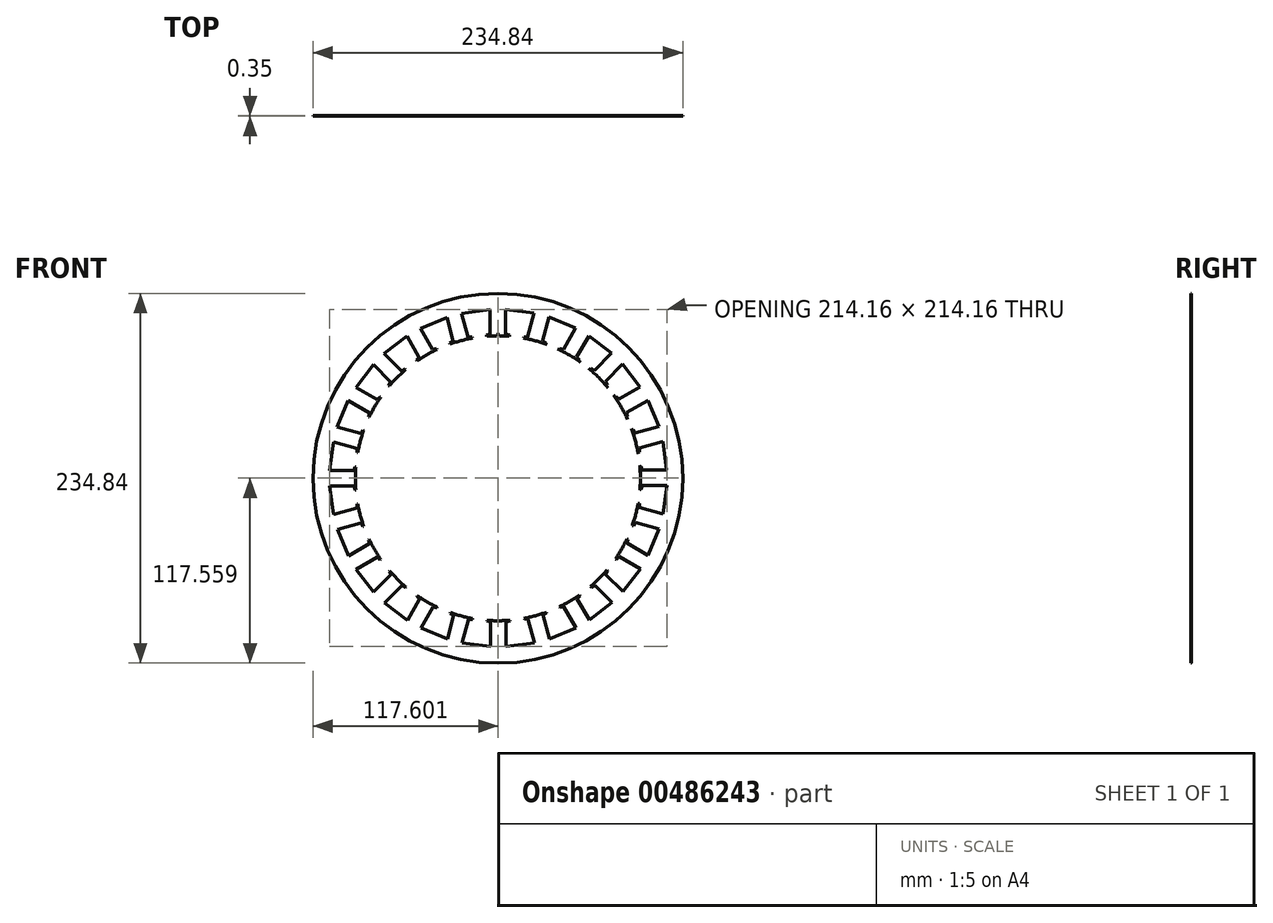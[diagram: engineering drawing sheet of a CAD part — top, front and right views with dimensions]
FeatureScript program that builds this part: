
annotation { "Feature Type Name" : "Feature", "Feature Type Description" : "" }
export const myFeature = defineFeature(function(context is Context, id is Id, definition is map)
    precondition{}
    {
        {
            var Q0;
            Q0=qCreatedBy(makeId("Front.planeOp"),FACE);
            var sketch = newSketch(context, id + "F0", { "sketchPlane" : qUnion([Q0])});
            skCircle(sketch, "E0", {"center": v(0, 0) * mm, "radius": 117.42 * mm});
            skCircle(sketch, "E1", {"center": v(0, 0) * mm, "radius": 90.5 * mm});
            skSolve(sketch);
        }
        {
            var Q0;
            Q0=makeQuery(id+"F0.imprint","IMPRINT",FACE,{"disambiguationData":[TD([[makeQuery(id+"F0.imprint","IMPRINT",EDGE,{"derivedFrom":sQuery(id+"F0.wireOp",EDGE,"E0")}),1.0]])]});
            extrude(context, id + "F1", {"entities" : qUnion([Q0]), "depth" : 0.35 * mm});
        }
        {
            var Q0;
            Q0=makeQuery(id+"F1.opExtrude","CAP_FACE",FACE,{"disambiguationData":[OSD([sQuery(id+"F0.wireOp",EDGE,"E0"),sQuery(id+"F0.wireOp",EDGE,"E1")])],"isStart":false});
            var sketch = newSketch(context, id + "F2", { "sketchPlane" : qUnion([Q0])});
            skLineSegment(sketch, "E2", {"start": v(0, 117.42) * mm, "end": v(0, 0) * mm, "construction": true});
            skLineSegment(sketch, "E3", {"start": v(0, 0) * mm, "end": v(15.9, 120.74) * mm, "construction": true});
            skLineSegment(sketch, "E4", {"start": v(7.35, 90.2) * mm, "end": v(7.35, 91) * mm});
            skLineSegment(sketch, "E5", {"start": v(7.35, 91) * mm, "end": v(4.94, 91.66) * mm});
            skLineSegment(sketch, "E6", {"start": v(4.94, 91.66) * mm, "end": v(4.94, 107.22) * mm});
            skLineSegment(sketch, "E7", {"start": v(4.94, 107.22) * mm, "end": v(13.96, 106.03) * mm});
            skLineSegment(sketch, "E8.MirrorCS", {"start": v(22.98, 104.85) * mm, "end": v(13.96, 106.03) * mm});
            skLineSegment(sketch, "E9.MirrorCS", {"start": v(18.95, 89.82) * mm, "end": v(22.98, 104.85) * mm});
            skLineSegment(sketch, "E10.MirrorCS", {"start": v(16.45, 89.8) * mm, "end": v(18.95, 89.82) * mm});
            skLineSegment(sketch, "E11.MirrorCS", {"start": v(16.25, 89.03) * mm, "end": v(16.45, 89.8) * mm});
            skLineSegment(sketch, "E12", {"start": v(7.35, 90.2) * mm, "end": v(16.25, 89.03) * mm});
            skLineSegment(sketch, "E13.1.0", {"start": v(-18.9, 89.77) * mm, "end": v(-22.94, 104.8) * mm});
            skLineSegment(sketch, "E13.1.1", {"start": v(-22.94, 104.8) * mm, "end": v(-13.92, 106) * mm});
            skLineSegment(sketch, "E13.1.2", {"start": v(-4.9, 107.18) * mm, "end": v(-13.92, 106) * mm});
            skLineSegment(sketch, "E13.1.3", {"start": v(-4.9, 91.62) * mm, "end": v(-4.9, 107.18) * mm});
            skLineSegment(sketch, "E13.1.4", {"start": v(-7.3, 90.96) * mm, "end": v(-4.9, 91.62) * mm});
            skLineSegment(sketch, "E13.1.5", {"start": v(-7.3, 90.16) * mm, "end": v(-7.3, 90.96) * mm});
            skLineSegment(sketch, "E13.1.6", {"start": v(-16.2, 88.99) * mm, "end": v(-7.3, 90.16) * mm});
            skLineSegment(sketch, "E13.1.7", {"start": v(-16.2, 88.99) * mm, "end": v(-16.41, 89.76) * mm});
            skLineSegment(sketch, "E13.1.8", {"start": v(-16.41, 89.76) * mm, "end": v(-18.9, 89.77) * mm});
            skLineSegment(sketch, "E13.2.0", {"start": v(-41.46, 81.78) * mm, "end": v(-49.24, 95.25) * mm});
            skLineSegment(sketch, "E13.2.1", {"start": v(-49.24, 95.25) * mm, "end": v(-40.83, 98.74) * mm});
            skLineSegment(sketch, "E13.2.2", {"start": v(-32.43, 102.22) * mm, "end": v(-40.83, 98.74) * mm});
            skLineSegment(sketch, "E13.2.3", {"start": v(-28.4, 87.19) * mm, "end": v(-32.43, 102.22) * mm});
            skLineSegment(sketch, "E13.2.4", {"start": v(-30.56, 85.93) * mm, "end": v(-28.4, 87.19) * mm});
            skLineSegment(sketch, "E13.2.5", {"start": v(-30.35, 85.15) * mm, "end": v(-30.56, 85.93) * mm});
            skLineSegment(sketch, "E13.2.6", {"start": v(-38.64, 81.72) * mm, "end": v(-30.35, 85.15) * mm});
            skLineSegment(sketch, "E13.2.7", {"start": v(-38.64, 81.72) * mm, "end": v(-39.04, 82.41) * mm});
            skLineSegment(sketch, "E13.2.8", {"start": v(-39.04, 82.41) * mm, "end": v(-41.46, 81.78) * mm});
            skLineSegment(sketch, "E13.3.0", {"start": v(-61.17, 68.22) * mm, "end": v(-72.17, 79.22) * mm});
            skLineSegment(sketch, "E13.3.1", {"start": v(-72.17, 79.22) * mm, "end": v(-64.96, 84.76) * mm});
            skLineSegment(sketch, "E13.3.2", {"start": v(-57.74, 90.3) * mm, "end": v(-64.96, 84.76) * mm});
            skLineSegment(sketch, "E13.3.3", {"start": v(-49.96, 76.82) * mm, "end": v(-57.74, 90.3) * mm});
            skLineSegment(sketch, "E13.3.4", {"start": v(-51.71, 75.05) * mm, "end": v(-49.96, 76.82) * mm});
            skLineSegment(sketch, "E13.3.5", {"start": v(-51.31, 74.35) * mm, "end": v(-51.71, 75.05) * mm});
            skLineSegment(sketch, "E13.3.6", {"start": v(-58.43, 68.9) * mm, "end": v(-51.31, 74.35) * mm});
            skLineSegment(sketch, "E13.3.7", {"start": v(-58.43, 68.9) * mm, "end": v(-59, 69.46) * mm});
            skLineSegment(sketch, "E13.3.8", {"start": v(-59, 69.46) * mm, "end": v(-61.17, 68.22) * mm});
            skLineSegment(sketch, "E13.4.0", {"start": v(-76.7, 50.02) * mm, "end": v(-90.18, 57.8) * mm});
            skLineSegment(sketch, "E13.4.1", {"start": v(-90.18, 57.8) * mm, "end": v(-84.64, 65.02) * mm});
            skLineSegment(sketch, "E13.4.2", {"start": v(-79.1, 72.24) * mm, "end": v(-84.64, 65.02) * mm});
            skLineSegment(sketch, "E13.4.3", {"start": v(-68.1, 61.23) * mm, "end": v(-79.1, 72.24) * mm});
            skLineSegment(sketch, "E13.4.4", {"start": v(-69.33, 59.06) * mm, "end": v(-68.1, 61.23) * mm});
            skLineSegment(sketch, "E13.4.5", {"start": v(-68.77, 58.5) * mm, "end": v(-69.33, 59.06) * mm});
            skLineSegment(sketch, "E13.4.6", {"start": v(-74.23, 51.38) * mm, "end": v(-68.77, 58.5) * mm});
            skLineSegment(sketch, "E13.4.7", {"start": v(-74.23, 51.38) * mm, "end": v(-74.92, 51.78) * mm});
            skLineSegment(sketch, "E13.4.8", {"start": v(-74.92, 51.78) * mm, "end": v(-76.7, 50.02) * mm});
            skLineSegment(sketch, "E13.5.0", {"start": v(-87, 28.42) * mm, "end": v(-102.02, 32.45) * mm});
            skLineSegment(sketch, "E13.5.1", {"start": v(-102.02, 32.45) * mm, "end": v(-98.54, 40.86) * mm});
            skLineSegment(sketch, "E13.5.2", {"start": v(-95.06, 49.26) * mm, "end": v(-98.54, 40.86) * mm});
            skLineSegment(sketch, "E13.5.3", {"start": v(-81.58, 41.48) * mm, "end": v(-95.06, 49.26) * mm});
            skLineSegment(sketch, "E13.5.4", {"start": v(-82.22, 39.06) * mm, "end": v(-81.58, 41.48) * mm});
            skLineSegment(sketch, "E13.5.5", {"start": v(-81.52, 38.66) * mm, "end": v(-82.22, 39.06) * mm});
            skLineSegment(sketch, "E13.5.6", {"start": v(-84.96, 30.37) * mm, "end": v(-81.52, 38.66) * mm});
            skLineSegment(sketch, "E13.5.7", {"start": v(-84.96, 30.37) * mm, "end": v(-85.73, 30.58) * mm});
            skLineSegment(sketch, "E13.5.8", {"start": v(-85.73, 30.58) * mm, "end": v(-87, 28.42) * mm});
            skLineSegment(sketch, "E13.6.0", {"start": v(-91.34, 4.9) * mm, "end": v(-106.9, 4.9) * mm});
            skLineSegment(sketch, "E13.6.1", {"start": v(-106.9, 4.9) * mm, "end": v(-105.71, 13.92) * mm});
            skLineSegment(sketch, "E13.6.2", {"start": v(-104.53, 22.94) * mm, "end": v(-105.71, 13.92) * mm});
            skLineSegment(sketch, "E13.6.3", {"start": v(-89.5, 18.9) * mm, "end": v(-104.53, 22.94) * mm});
            skLineSegment(sketch, "E13.6.4", {"start": v(-89.48, 16.41) * mm, "end": v(-89.5, 18.9) * mm});
            skLineSegment(sketch, "E13.6.5", {"start": v(-88.71, 16.2) * mm, "end": v(-89.48, 16.41) * mm});
            skLineSegment(sketch, "E13.6.6", {"start": v(-89.88, 7.3) * mm, "end": v(-88.71, 16.2) * mm});
            skLineSegment(sketch, "E13.6.7", {"start": v(-89.88, 7.3) * mm, "end": v(-90.68, 7.3) * mm});
            skLineSegment(sketch, "E13.6.8", {"start": v(-90.68, 7.3) * mm, "end": v(-91.34, 4.9) * mm});
            skLineSegment(sketch, "E13.7.0", {"start": v(-89.45, -18.95) * mm, "end": v(-104.48, -22.98) * mm});
            skLineSegment(sketch, "E13.7.1", {"start": v(-104.48, -22.98) * mm, "end": v(-105.67, -13.96) * mm});
            skLineSegment(sketch, "E13.7.2", {"start": v(-106.86, -4.94) * mm, "end": v(-105.67, -13.96) * mm});
            skLineSegment(sketch, "E13.7.3", {"start": v(-91.3, -4.94) * mm, "end": v(-106.86, -4.94) * mm});
            skLineSegment(sketch, "E13.7.4", {"start": v(-90.64, -7.35) * mm, "end": v(-91.3, -4.94) * mm});
            skLineSegment(sketch, "E13.7.5", {"start": v(-89.84, -7.35) * mm, "end": v(-90.64, -7.35) * mm});
            skLineSegment(sketch, "E13.7.6", {"start": v(-88.67, -16.25) * mm, "end": v(-89.84, -7.35) * mm});
            skLineSegment(sketch, "E13.7.7", {"start": v(-88.67, -16.25) * mm, "end": v(-89.44, -16.45) * mm});
            skLineSegment(sketch, "E13.7.8", {"start": v(-89.44, -16.45) * mm, "end": v(-89.45, -18.95) * mm});
            skLineSegment(sketch, "E13.8.0", {"start": v(-81.46, -41.5) * mm, "end": v(-94.93, -49.28) * mm});
            skLineSegment(sketch, "E13.8.1", {"start": v(-94.93, -49.28) * mm, "end": v(-98.42, -40.88) * mm});
            skLineSegment(sketch, "E13.8.2", {"start": v(-101.9, -32.47) * mm, "end": v(-98.42, -40.88) * mm});
            skLineSegment(sketch, "E13.8.3", {"start": v(-86.87, -28.44) * mm, "end": v(-101.9, -32.47) * mm});
            skLineSegment(sketch, "E13.8.4", {"start": v(-85.6, -30.6) * mm, "end": v(-86.87, -28.44) * mm});
            skLineSegment(sketch, "E13.8.5", {"start": v(-84.83, -30.4) * mm, "end": v(-85.6, -30.6) * mm});
            skLineSegment(sketch, "E13.8.6", {"start": v(-81.4, -38.68) * mm, "end": v(-84.83, -30.4) * mm});
            skLineSegment(sketch, "E13.8.7", {"start": v(-81.4, -38.68) * mm, "end": v(-82.1, -39.08) * mm});
            skLineSegment(sketch, "E13.8.8", {"start": v(-82.1, -39.08) * mm, "end": v(-81.46, -41.5) * mm});
            skLineSegment(sketch, "E13.9.0", {"start": v(-67.9, -61.21) * mm, "end": v(-78.9, -72.21) * mm});
            skLineSegment(sketch, "E13.9.1", {"start": v(-78.9, -72.21) * mm, "end": v(-84.44, -65) * mm});
            skLineSegment(sketch, "E13.9.2", {"start": v(-89.98, -57.78) * mm, "end": v(-84.44, -65) * mm});
            skLineSegment(sketch, "E13.9.3", {"start": v(-76.5, -50) * mm, "end": v(-89.98, -57.78) * mm});
            skLineSegment(sketch, "E13.9.4", {"start": v(-74.73, -51.76) * mm, "end": v(-76.5, -50) * mm});
            skLineSegment(sketch, "E13.9.5", {"start": v(-74.03, -51.36) * mm, "end": v(-74.73, -51.76) * mm});
            skLineSegment(sketch, "E13.9.6", {"start": v(-68.57, -58.48) * mm, "end": v(-74.03, -51.36) * mm});
            skLineSegment(sketch, "E13.9.7", {"start": v(-68.57, -58.48) * mm, "end": v(-69.14, -59.04) * mm});
            skLineSegment(sketch, "E13.9.8", {"start": v(-69.14, -59.04) * mm, "end": v(-67.9, -61.21) * mm});
            skLineSegment(sketch, "E13.10.0", {"start": v(-49.7, -76.74) * mm, "end": v(-57.48, -90.22) * mm});
            skLineSegment(sketch, "E13.10.1", {"start": v(-57.48, -90.22) * mm, "end": v(-64.7, -84.68) * mm});
            skLineSegment(sketch, "E13.10.2", {"start": v(-71.92, -79.14) * mm, "end": v(-64.7, -84.68) * mm});
            skLineSegment(sketch, "E13.10.3", {"start": v(-60.91, -68.14) * mm, "end": v(-71.92, -79.14) * mm});
            skLineSegment(sketch, "E13.10.4", {"start": v(-58.74, -69.38) * mm, "end": v(-60.91, -68.14) * mm});
            skLineSegment(sketch, "E13.10.5", {"start": v(-58.18, -68.81) * mm, "end": v(-58.74, -69.38) * mm});
            skLineSegment(sketch, "E13.10.6", {"start": v(-51.06, -74.27) * mm, "end": v(-58.18, -68.81) * mm});
            skLineSegment(sketch, "E13.10.7", {"start": v(-51.06, -74.27) * mm, "end": v(-51.46, -74.97) * mm});
            skLineSegment(sketch, "E13.10.8", {"start": v(-51.46, -74.97) * mm, "end": v(-49.7, -76.74) * mm});
            skLineSegment(sketch, "E13.11.0", {"start": v(-28.1, -87.03) * mm, "end": v(-32.13, -102.06) * mm});
            skLineSegment(sketch, "E13.11.1", {"start": v(-32.13, -102.06) * mm, "end": v(-40.54, -98.58) * mm});
            skLineSegment(sketch, "E13.11.2", {"start": v(-48.94, -95.1) * mm, "end": v(-40.54, -98.58) * mm});
            skLineSegment(sketch, "E13.11.3", {"start": v(-41.16, -81.62) * mm, "end": v(-48.94, -95.1) * mm});
            skLineSegment(sketch, "E13.11.4", {"start": v(-38.74, -82.26) * mm, "end": v(-41.16, -81.62) * mm});
            skLineSegment(sketch, "E13.11.5", {"start": v(-38.34, -81.57) * mm, "end": v(-38.74, -82.26) * mm});
            skLineSegment(sketch, "E13.11.6", {"start": v(-30.05, -85) * mm, "end": v(-38.34, -81.57) * mm});
            skLineSegment(sketch, "E13.11.7", {"start": v(-30.05, -85) * mm, "end": v(-30.26, -85.77) * mm});
            skLineSegment(sketch, "E13.11.8", {"start": v(-30.26, -85.77) * mm, "end": v(-28.1, -87.03) * mm});
            skLineSegment(sketch, "E13.12.0", {"start": v(-4.58, -91.38) * mm, "end": v(-4.58, -106.94) * mm});
            skLineSegment(sketch, "E13.12.1", {"start": v(-4.58, -106.94) * mm, "end": v(-13.6, -105.76) * mm});
            skLineSegment(sketch, "E13.12.2", {"start": v(-22.62, -104.57) * mm, "end": v(-13.6, -105.76) * mm});
            skLineSegment(sketch, "E13.12.3", {"start": v(-18.6, -89.54) * mm, "end": v(-22.62, -104.57) * mm});
            skLineSegment(sketch, "E13.12.4", {"start": v(-16.1, -89.53) * mm, "end": v(-18.6, -89.54) * mm});
            skLineSegment(sketch, "E13.12.5", {"start": v(-15.88, -88.75) * mm, "end": v(-16.1, -89.53) * mm});
            skLineSegment(sketch, "E13.12.6", {"start": v(-6.99, -89.92) * mm, "end": v(-15.88, -88.75) * mm});
            skLineSegment(sketch, "E13.12.7", {"start": v(-6.99, -89.92) * mm, "end": v(-6.99, -90.72) * mm});
            skLineSegment(sketch, "E13.12.8", {"start": v(-6.99, -90.72) * mm, "end": v(-4.58, -91.38) * mm});
            skLineSegment(sketch, "E13.13.0", {"start": v(19.27, -89.5) * mm, "end": v(23.3, -104.53) * mm});
            skLineSegment(sketch, "E13.13.1", {"start": v(23.3, -104.53) * mm, "end": v(14.28, -105.71) * mm});
            skLineSegment(sketch, "E13.13.2", {"start": v(5.26, -106.9) * mm, "end": v(14.28, -105.71) * mm});
            skLineSegment(sketch, "E13.13.3", {"start": v(5.26, -91.34) * mm, "end": v(5.26, -106.9) * mm});
            skLineSegment(sketch, "E13.13.4", {"start": v(7.67, -90.68) * mm, "end": v(5.26, -91.34) * mm});
            skLineSegment(sketch, "E13.13.5", {"start": v(7.67, -89.88) * mm, "end": v(7.67, -90.68) * mm});
            skLineSegment(sketch, "E13.13.6", {"start": v(16.57, -88.71) * mm, "end": v(7.67, -89.88) * mm});
            skLineSegment(sketch, "E13.13.7", {"start": v(16.57, -88.71) * mm, "end": v(16.77, -89.48) * mm});
            skLineSegment(sketch, "E13.13.8", {"start": v(16.77, -89.48) * mm, "end": v(19.27, -89.5) * mm});
            skLineSegment(sketch, "E13.14.0", {"start": v(41.82, -81.5) * mm, "end": v(49.6, -94.98) * mm});
            skLineSegment(sketch, "E13.14.1", {"start": v(49.6, -94.98) * mm, "end": v(41.2, -98.46) * mm});
            skLineSegment(sketch, "E13.14.2", {"start": v(32.8, -101.94) * mm, "end": v(41.2, -98.46) * mm});
            skLineSegment(sketch, "E13.14.3", {"start": v(28.76, -86.9) * mm, "end": v(32.8, -101.94) * mm});
            skLineSegment(sketch, "E13.14.4", {"start": v(30.92, -85.65) * mm, "end": v(28.76, -86.9) * mm});
            skLineSegment(sketch, "E13.14.5", {"start": v(30.71, -84.88) * mm, "end": v(30.92, -85.65) * mm});
            skLineSegment(sketch, "E13.14.6", {"start": v(39, -81.44) * mm, "end": v(30.71, -84.88) * mm});
            skLineSegment(sketch, "E13.14.7", {"start": v(39, -81.44) * mm, "end": v(39.4, -82.13) * mm});
            skLineSegment(sketch, "E13.14.8", {"start": v(39.4, -82.13) * mm, "end": v(41.82, -81.5) * mm});
            skLineSegment(sketch, "E13.15.0", {"start": v(61.53, -67.94) * mm, "end": v(72.53, -78.95) * mm});
            skLineSegment(sketch, "E13.15.1", {"start": v(72.53, -78.95) * mm, "end": v(65.32, -84.48) * mm});
            skLineSegment(sketch, "E13.15.2", {"start": v(58.1, -90.02) * mm, "end": v(65.32, -84.48) * mm});
            skLineSegment(sketch, "E13.15.3", {"start": v(50.32, -76.55) * mm, "end": v(58.1, -90.02) * mm});
            skLineSegment(sketch, "E13.15.4", {"start": v(52.08, -74.77) * mm, "end": v(50.32, -76.55) * mm});
            skLineSegment(sketch, "E13.15.5", {"start": v(51.68, -74.08) * mm, "end": v(52.08, -74.77) * mm});
            skLineSegment(sketch, "E13.15.6", {"start": v(58.8, -68.61) * mm, "end": v(51.68, -74.08) * mm});
            skLineSegment(sketch, "E13.15.7", {"start": v(58.8, -68.61) * mm, "end": v(59.36, -69.18) * mm});
            skLineSegment(sketch, "E13.15.8", {"start": v(59.36, -69.18) * mm, "end": v(61.53, -67.94) * mm});
            skLineSegment(sketch, "E13.16.0", {"start": v(77.06, -49.74) * mm, "end": v(90.54, -57.52) * mm});
            skLineSegment(sketch, "E13.16.1", {"start": v(90.54, -57.52) * mm, "end": v(85, -64.74) * mm});
            skLineSegment(sketch, "E13.16.2", {"start": v(79.46, -71.96) * mm, "end": v(85, -64.74) * mm});
            skLineSegment(sketch, "E13.16.3", {"start": v(68.46, -60.96) * mm, "end": v(79.46, -71.96) * mm});
            skLineSegment(sketch, "E13.16.4", {"start": v(69.7, -58.79) * mm, "end": v(68.46, -60.96) * mm});
            skLineSegment(sketch, "E13.16.5", {"start": v(69.13, -58.22) * mm, "end": v(69.7, -58.79) * mm});
            skLineSegment(sketch, "E13.16.6", {"start": v(74.6, -51.1) * mm, "end": v(69.13, -58.22) * mm});
            skLineSegment(sketch, "E13.16.7", {"start": v(74.6, -51.1) * mm, "end": v(75.29, -51.5) * mm});
            skLineSegment(sketch, "E13.16.8", {"start": v(75.29, -51.5) * mm, "end": v(77.06, -49.74) * mm});
            skLineSegment(sketch, "E13.17.0", {"start": v(87.35, -28.15) * mm, "end": v(102.38, -32.17) * mm});
            skLineSegment(sketch, "E13.17.1", {"start": v(102.38, -32.17) * mm, "end": v(98.9, -40.58) * mm});
            skLineSegment(sketch, "E13.17.2", {"start": v(95.42, -48.98) * mm, "end": v(98.9, -40.58) * mm});
            skLineSegment(sketch, "E13.17.3", {"start": v(81.94, -41.2) * mm, "end": v(95.42, -48.98) * mm});
            skLineSegment(sketch, "E13.17.4", {"start": v(82.58, -38.79) * mm, "end": v(81.94, -41.2) * mm});
            skLineSegment(sketch, "E13.17.5", {"start": v(81.89, -38.39) * mm, "end": v(82.58, -38.79) * mm});
            skLineSegment(sketch, "E13.17.6", {"start": v(85.32, -30.1) * mm, "end": v(81.89, -38.39) * mm});
            skLineSegment(sketch, "E13.17.7", {"start": v(85.32, -30.1) * mm, "end": v(86.1, -30.3) * mm});
            skLineSegment(sketch, "E13.17.8", {"start": v(86.1, -30.3) * mm, "end": v(87.35, -28.15) * mm});
            skLineSegment(sketch, "E13.18.0", {"start": v(91.7, -4.62) * mm, "end": v(107.26, -4.62) * mm});
            skLineSegment(sketch, "E13.18.1", {"start": v(107.26, -4.62) * mm, "end": v(106.08, -13.64) * mm});
            skLineSegment(sketch, "E13.18.2", {"start": v(104.89, -22.66) * mm, "end": v(106.08, -13.64) * mm});
            skLineSegment(sketch, "E13.18.3", {"start": v(89.86, -18.63) * mm, "end": v(104.89, -22.66) * mm});
            skLineSegment(sketch, "E13.18.4", {"start": v(89.84, -16.13) * mm, "end": v(89.86, -18.63) * mm});
            skLineSegment(sketch, "E13.18.5", {"start": v(89.07, -15.93) * mm, "end": v(89.84, -16.13) * mm});
            skLineSegment(sketch, "E13.18.6", {"start": v(90.24, -7.03) * mm, "end": v(89.07, -15.93) * mm});
            skLineSegment(sketch, "E13.18.7", {"start": v(90.24, -7.03) * mm, "end": v(91.04, -7.03) * mm});
            skLineSegment(sketch, "E13.18.8", {"start": v(91.04, -7.03) * mm, "end": v(91.7, -4.62) * mm});
            skLineSegment(sketch, "E13.19.0", {"start": v(89.82, 19.23) * mm, "end": v(104.85, 23.26) * mm});
            skLineSegment(sketch, "E13.19.1", {"start": v(104.85, 23.26) * mm, "end": v(106.03, 14.24) * mm});
            skLineSegment(sketch, "E13.19.2", {"start": v(107.22, 5.22) * mm, "end": v(106.03, 14.24) * mm});
            skLineSegment(sketch, "E13.19.3", {"start": v(91.66, 5.22) * mm, "end": v(107.22, 5.22) * mm});
            skLineSegment(sketch, "E13.19.4", {"start": v(91, 7.63) * mm, "end": v(91.66, 5.22) * mm});
            skLineSegment(sketch, "E13.19.5", {"start": v(90.2, 7.63) * mm, "end": v(91, 7.63) * mm});
            skLineSegment(sketch, "E13.19.6", {"start": v(89.03, 16.52) * mm, "end": v(90.2, 7.63) * mm});
            skLineSegment(sketch, "E13.19.7", {"start": v(89.03, 16.52) * mm, "end": v(89.8, 16.73) * mm});
            skLineSegment(sketch, "E13.19.8", {"start": v(89.8, 16.73) * mm, "end": v(89.82, 19.23) * mm});
            skLineSegment(sketch, "E13.20.0", {"start": v(81.82, 41.78) * mm, "end": v(95.3, 49.56) * mm});
            skLineSegment(sketch, "E13.20.1", {"start": v(95.3, 49.56) * mm, "end": v(98.78, 41.15) * mm});
            skLineSegment(sketch, "E13.20.2", {"start": v(102.26, 32.75) * mm, "end": v(98.78, 41.15) * mm});
            skLineSegment(sketch, "E13.20.3", {"start": v(87.23, 28.72) * mm, "end": v(102.26, 32.75) * mm});
            skLineSegment(sketch, "E13.20.4", {"start": v(85.97, 30.88) * mm, "end": v(87.23, 28.72) * mm});
            skLineSegment(sketch, "E13.20.5", {"start": v(85.2, 30.67) * mm, "end": v(85.97, 30.88) * mm});
            skLineSegment(sketch, "E13.20.6", {"start": v(81.76, 38.96) * mm, "end": v(85.2, 30.67) * mm});
            skLineSegment(sketch, "E13.20.7", {"start": v(81.76, 38.96) * mm, "end": v(82.45, 39.36) * mm});
            skLineSegment(sketch, "E13.20.8", {"start": v(82.45, 39.36) * mm, "end": v(81.82, 41.78) * mm});
            skLineSegment(sketch, "E13.21.0", {"start": v(68.26, 61.49) * mm, "end": v(79.26, 72.5) * mm});
            skLineSegment(sketch, "E13.21.1", {"start": v(79.26, 72.5) * mm, "end": v(84.8, 65.27) * mm});
            skLineSegment(sketch, "E13.21.2", {"start": v(90.34, 58.06) * mm, "end": v(84.8, 65.27) * mm});
            skLineSegment(sketch, "E13.21.3", {"start": v(76.87, 50.28) * mm, "end": v(90.34, 58.06) * mm});
            skLineSegment(sketch, "E13.21.4", {"start": v(75.09, 52.03) * mm, "end": v(76.87, 50.28) * mm});
            skLineSegment(sketch, "E13.21.5", {"start": v(74.4, 51.63) * mm, "end": v(75.09, 52.03) * mm});
            skLineSegment(sketch, "E13.21.6", {"start": v(68.93, 58.75) * mm, "end": v(74.4, 51.63) * mm});
            skLineSegment(sketch, "E13.21.7", {"start": v(68.93, 58.75) * mm, "end": v(69.5, 59.32) * mm});
            skLineSegment(sketch, "E13.21.8", {"start": v(69.5, 59.32) * mm, "end": v(68.26, 61.49) * mm});
            skLineSegment(sketch, "E13.22.0", {"start": v(50.06, 77.02) * mm, "end": v(57.84, 90.5) * mm});
            skLineSegment(sketch, "E13.22.1", {"start": v(57.84, 90.5) * mm, "end": v(65.06, 84.96) * mm});
            skLineSegment(sketch, "E13.22.2", {"start": v(72.28, 79.42) * mm, "end": v(65.06, 84.96) * mm});
            skLineSegment(sketch, "E13.22.3", {"start": v(61.28, 68.42) * mm, "end": v(72.28, 79.42) * mm});
            skLineSegment(sketch, "E13.22.4", {"start": v(59.1, 69.65) * mm, "end": v(61.28, 68.42) * mm});
            skLineSegment(sketch, "E13.22.5", {"start": v(58.54, 69.09) * mm, "end": v(59.1, 69.65) * mm});
            skLineSegment(sketch, "E13.22.6", {"start": v(51.42, 74.55) * mm, "end": v(58.54, 69.09) * mm});
            skLineSegment(sketch, "E13.22.7", {"start": v(51.42, 74.55) * mm, "end": v(51.82, 75.24) * mm});
            skLineSegment(sketch, "E13.22.8", {"start": v(51.82, 75.24) * mm, "end": v(50.06, 77.02) * mm});
            skLineSegment(sketch, "E13.23.0", {"start": v(28.47, 87.31) * mm, "end": v(32.5, 102.34) * mm});
            skLineSegment(sketch, "E13.23.1", {"start": v(32.5, 102.34) * mm, "end": v(40.9, 98.86) * mm});
            skLineSegment(sketch, "E13.23.2", {"start": v(49.3, 95.38) * mm, "end": v(40.9, 98.86) * mm});
            skLineSegment(sketch, "E13.23.3", {"start": v(41.52, 81.9) * mm, "end": v(49.3, 95.38) * mm});
            skLineSegment(sketch, "E13.23.4", {"start": v(39.1, 82.54) * mm, "end": v(41.52, 81.9) * mm});
            skLineSegment(sketch, "E13.23.5", {"start": v(38.7, 81.84) * mm, "end": v(39.1, 82.54) * mm});
            skLineSegment(sketch, "E13.23.6", {"start": v(30.42, 85.28) * mm, "end": v(38.7, 81.84) * mm});
            skLineSegment(sketch, "E13.23.7", {"start": v(30.42, 85.28) * mm, "end": v(30.62, 86.05) * mm});
            skLineSegment(sketch, "E13.23.8", {"start": v(30.62, 86.05) * mm, "end": v(28.47, 87.31) * mm});
            skPoint(sketch, "E13.center", {"position": v(0.18, 0.14) * mm});
            skSolve(sketch);
        }
        {
            var Q0;
            {var subQ0=sQuery(id+"F2.wireOp",EDGE,"E4");Q0=makeQuery(id+"F2.imprint","IMPRINT",FACE,{"disambiguationData":[TD([[makeQuery(id+"F2.imprint","IMPRINT",EDGE,{"derivedFrom":subQ0}),-1.0]])]});}
            var Q1;
            Q1=makeQuery(id+"F2.imprint","IMPRINT",FACE,{"disambiguationData":[TD([[makeQuery(id+"F2.imprint","IMPRINT",EDGE,{"derivedFrom":sQuery(id+"F2.wireOp",EDGE,"E13.1.0")}),-1.0]])]});
            var Q2;
            Q2=makeQuery(id+"F2.imprint","IMPRINT",FACE,{"disambiguationData":[TD([[makeQuery(id+"F2.imprint","IMPRINT",EDGE,{"derivedFrom":sQuery(id+"F2.wireOp",EDGE,"E13.2.0")}),-1.0]])]});
            var Q3;
            Q3=makeQuery(id+"F2.imprint","IMPRINT",FACE,{"disambiguationData":[TD([[makeQuery(id+"F2.imprint","IMPRINT",EDGE,{"derivedFrom":sQuery(id+"F2.wireOp",EDGE,"E13.3.0")}),-1.0]])]});
            var Q4;
            Q4=makeQuery(id+"F2.imprint","IMPRINT",FACE,{"disambiguationData":[TD([[makeQuery(id+"F2.imprint","IMPRINT",EDGE,{"derivedFrom":sQuery(id+"F2.wireOp",EDGE,"E13.4.0")}),-1.0]])]});
            var Q5;
            Q5=makeQuery(id+"F2.imprint","IMPRINT",FACE,{"disambiguationData":[TD([[makeQuery(id+"F2.imprint","IMPRINT",EDGE,{"derivedFrom":sQuery(id+"F2.wireOp",EDGE,"E13.5.0")}),-1.0]])]});
            var Q6;
            Q6=makeQuery(id+"F2.imprint","IMPRINT",FACE,{"disambiguationData":[TD([[makeQuery(id+"F2.imprint","IMPRINT",EDGE,{"derivedFrom":sQuery(id+"F2.wireOp",EDGE,"E13.6.0")}),-1.0]])]});
            var Q7;
            Q7=makeQuery(id+"F2.imprint","IMPRINT",FACE,{"disambiguationData":[TD([[makeQuery(id+"F2.imprint","IMPRINT",EDGE,{"derivedFrom":sQuery(id+"F2.wireOp",EDGE,"E13.7.0")}),-1.0]])]});
            var Q8;
            Q8=makeQuery(id+"F2.imprint","IMPRINT",FACE,{"disambiguationData":[TD([[makeQuery(id+"F2.imprint","IMPRINT",EDGE,{"derivedFrom":sQuery(id+"F2.wireOp",EDGE,"E13.8.0")}),-1.0]])]});
            var Q9;
            Q9=makeQuery(id+"F2.imprint","IMPRINT",FACE,{"disambiguationData":[TD([[makeQuery(id+"F2.imprint","IMPRINT",EDGE,{"derivedFrom":sQuery(id+"F2.wireOp",EDGE,"E13.9.0")}),-1.0]])]});
            var Q10;
            Q10=makeQuery(id+"F2.imprint","IMPRINT",FACE,{"disambiguationData":[TD([[makeQuery(id+"F2.imprint","IMPRINT",EDGE,{"derivedFrom":sQuery(id+"F2.wireOp",EDGE,"E13.10.0")}),-1.0]])]});
            var Q11;
            Q11=makeQuery(id+"F2.imprint","IMPRINT",FACE,{"disambiguationData":[TD([[makeQuery(id+"F2.imprint","IMPRINT",EDGE,{"derivedFrom":sQuery(id+"F2.wireOp",EDGE,"E13.11.0")}),-1.0]])]});
            var Q12;
            Q12=makeQuery(id+"F2.imprint","IMPRINT",FACE,{"disambiguationData":[TD([[makeQuery(id+"F2.imprint","IMPRINT",EDGE,{"derivedFrom":sQuery(id+"F2.wireOp",EDGE,"E13.12.0")}),-1.0]])]});
            var Q13;
            Q13=makeQuery(id+"F2.imprint","IMPRINT",FACE,{"disambiguationData":[TD([[makeQuery(id+"F2.imprint","IMPRINT",EDGE,{"derivedFrom":sQuery(id+"F2.wireOp",EDGE,"E13.13.0")}),-1.0]])]});
            var Q14;
            Q14=makeQuery(id+"F2.imprint","IMPRINT",FACE,{"disambiguationData":[TD([[makeQuery(id+"F2.imprint","IMPRINT",EDGE,{"derivedFrom":sQuery(id+"F2.wireOp",EDGE,"E13.14.0")}),-1.0]])]});
            var Q15;
            Q15=makeQuery(id+"F2.imprint","IMPRINT",FACE,{"disambiguationData":[TD([[makeQuery(id+"F2.imprint","IMPRINT",EDGE,{"derivedFrom":sQuery(id+"F2.wireOp",EDGE,"E13.15.0")}),-1.0]])]});
            var Q16;
            Q16=makeQuery(id+"F2.imprint","IMPRINT",FACE,{"disambiguationData":[TD([[makeQuery(id+"F2.imprint","IMPRINT",EDGE,{"derivedFrom":sQuery(id+"F2.wireOp",EDGE,"E13.16.0")}),-1.0]])]});
            var Q17;
            Q17=makeQuery(id+"F2.imprint","IMPRINT",FACE,{"disambiguationData":[TD([[makeQuery(id+"F2.imprint","IMPRINT",EDGE,{"derivedFrom":sQuery(id+"F2.wireOp",EDGE,"E13.17.0")}),-1.0]])]});
            var Q18;
            Q18=makeQuery(id+"F2.imprint","IMPRINT",FACE,{"disambiguationData":[TD([[makeQuery(id+"F2.imprint","IMPRINT",EDGE,{"derivedFrom":sQuery(id+"F2.wireOp",EDGE,"E13.18.0")}),-1.0]])]});
            var Q19;
            Q19=makeQuery(id+"F2.imprint","IMPRINT",FACE,{"disambiguationData":[TD([[makeQuery(id+"F2.imprint","IMPRINT",EDGE,{"derivedFrom":sQuery(id+"F2.wireOp",EDGE,"E13.19.0")}),-1.0]])]});
            var Q20;
            Q20=makeQuery(id+"F2.imprint","IMPRINT",FACE,{"disambiguationData":[TD([[makeQuery(id+"F2.imprint","IMPRINT",EDGE,{"derivedFrom":sQuery(id+"F2.wireOp",EDGE,"E13.20.0")}),-1.0]])]});
            var Q21;
            Q21=makeQuery(id+"F2.imprint","IMPRINT",FACE,{"disambiguationData":[TD([[makeQuery(id+"F2.imprint","IMPRINT",EDGE,{"derivedFrom":sQuery(id+"F2.wireOp",EDGE,"E13.21.0")}),-1.0]])]});
            var Q22;
            Q22=makeQuery(id+"F2.imprint","IMPRINT",FACE,{"disambiguationData":[TD([[makeQuery(id+"F2.imprint","IMPRINT",EDGE,{"derivedFrom":sQuery(id+"F2.wireOp",EDGE,"E13.22.0")}),-1.0]])]});
            var Q23;
            Q23=makeQuery(id+"F2.imprint","IMPRINT",FACE,{"disambiguationData":[TD([[makeQuery(id+"F2.imprint","IMPRINT",EDGE,{"derivedFrom":sQuery(id+"F2.wireOp",EDGE,"E13.23.0")}),-1.0]])]});
            extrude(context, id + "F3", {"entities" : qUnion([Q0, Q1, Q2, Q3, Q4, Q5, Q6, Q7, Q8, Q9, Q10, Q11, Q12, Q13, Q14, Q15, Q16, Q17, Q18, Q19, Q20, Q21, Q22, Q23]), "operationType" : NewBodyOperationType.REMOVE, "endBound" : BoundingType.THROUGH_ALL, "oppositeDirection" : true, "depth" : 25 * mm});
        }
        {
            var Q0;
            Q0=makeQuery(id+"F1.opExtrude","CAP_FACE",FACE,{"disambiguationData":[OSD([sQuery(id+"F0.wireOp",EDGE,"E0"),sQuery(id+"F0.wireOp",EDGE,"E1")])],"isStart":false});
            var sketch = newSketch(context, id + "F4", { "sketchPlane" : qUnion([Q0])});
            skLineSegment(sketch, "E14", {"start": v(0, 117.42) * mm, "end": v(0, 82.18) * mm, "construction": true});
            skLineSegment(sketch, "E15", {"start": v(1, 90.5) * mm, "end": v(1, 91.3) * mm});
            skLineSegment(sketch, "E16.MirrorCS", {"start": v(-1, 90.5) * mm, "end": v(-1, 91.3) * mm});
            skLineSegment(sketch, "E17", {"start": v(-1, 91.3) * mm, "end": v(1, 91.3) * mm});
            skLineSegment(sketch, "E18", {"start": v(-1, 90.5) * mm, "end": v(1, 90.5) * mm});
            skLineSegment(sketch, "E19.1.0", {"start": v(-24.39, 87.15) * mm, "end": v(-22.46, 87.67) * mm});
            skLineSegment(sketch, "E19.1.1", {"start": v(-24.39, 87.15) * mm, "end": v(-24.6, 87.93) * mm});
            skLineSegment(sketch, "E19.1.2", {"start": v(-24.6, 87.93) * mm, "end": v(-22.66, 88.45) * mm});
            skLineSegment(sketch, "E19.1.3", {"start": v(-22.46, 87.67) * mm, "end": v(-22.66, 88.45) * mm});
            skLineSegment(sketch, "E19.2.0", {"start": v(-46.11, 77.87) * mm, "end": v(-44.38, 78.87) * mm});
            skLineSegment(sketch, "E19.2.1", {"start": v(-46.11, 77.87) * mm, "end": v(-46.52, 78.57) * mm});
            skLineSegment(sketch, "E19.2.2", {"start": v(-46.52, 78.57) * mm, "end": v(-44.78, 79.57) * mm});
            skLineSegment(sketch, "E19.2.3", {"start": v(-44.38, 78.87) * mm, "end": v(-44.78, 79.57) * mm});
            skLineSegment(sketch, "E19.3.0", {"start": v(-64.7, 63.28) * mm, "end": v(-63.28, 64.7) * mm});
            skLineSegment(sketch, "E19.3.1", {"start": v(-64.7, 63.28) * mm, "end": v(-65.27, 63.85) * mm});
            skLineSegment(sketch, "E19.3.2", {"start": v(-65.27, 63.85) * mm, "end": v(-63.85, 65.27) * mm});
            skLineSegment(sketch, "E19.3.3", {"start": v(-63.28, 64.7) * mm, "end": v(-63.85, 65.27) * mm});
            skLineSegment(sketch, "E19.4.0", {"start": v(-78.87, 44.38) * mm, "end": v(-77.87, 46.11) * mm});
            skLineSegment(sketch, "E19.4.1", {"start": v(-78.87, 44.38) * mm, "end": v(-79.57, 44.78) * mm});
            skLineSegment(sketch, "E19.4.2", {"start": v(-79.57, 44.78) * mm, "end": v(-78.57, 46.52) * mm});
            skLineSegment(sketch, "E19.4.3", {"start": v(-77.87, 46.11) * mm, "end": v(-78.57, 46.52) * mm});
            skLineSegment(sketch, "E19.5.0", {"start": v(-87.67, 22.46) * mm, "end": v(-87.15, 24.39) * mm});
            skLineSegment(sketch, "E19.5.1", {"start": v(-87.67, 22.46) * mm, "end": v(-88.45, 22.66) * mm});
            skLineSegment(sketch, "E19.5.2", {"start": v(-88.45, 22.66) * mm, "end": v(-87.93, 24.6) * mm});
            skLineSegment(sketch, "E19.5.3", {"start": v(-87.15, 24.39) * mm, "end": v(-87.93, 24.6) * mm});
            skLineSegment(sketch, "E19.6.0", {"start": v(-90.5, -1) * mm, "end": v(-90.5, 1) * mm});
            skLineSegment(sketch, "E19.6.1", {"start": v(-90.5, -1) * mm, "end": v(-91.3, -1) * mm});
            skLineSegment(sketch, "E19.6.2", {"start": v(-91.3, -1) * mm, "end": v(-91.3, 1) * mm});
            skLineSegment(sketch, "E19.6.3", {"start": v(-90.5, 1) * mm, "end": v(-91.3, 1) * mm});
            skLineSegment(sketch, "E19.7.0", {"start": v(-87.15, -24.39) * mm, "end": v(-87.67, -22.46) * mm});
            skLineSegment(sketch, "E19.7.1", {"start": v(-87.15, -24.39) * mm, "end": v(-87.93, -24.6) * mm});
            skLineSegment(sketch, "E19.7.2", {"start": v(-87.93, -24.6) * mm, "end": v(-88.45, -22.66) * mm});
            skLineSegment(sketch, "E19.7.3", {"start": v(-87.67, -22.46) * mm, "end": v(-88.45, -22.66) * mm});
            skLineSegment(sketch, "E19.8.0", {"start": v(-77.87, -46.11) * mm, "end": v(-78.87, -44.38) * mm});
            skLineSegment(sketch, "E19.8.1", {"start": v(-77.87, -46.11) * mm, "end": v(-78.57, -46.52) * mm});
            skLineSegment(sketch, "E19.8.2", {"start": v(-78.57, -46.52) * mm, "end": v(-79.57, -44.78) * mm});
            skLineSegment(sketch, "E19.8.3", {"start": v(-78.87, -44.38) * mm, "end": v(-79.57, -44.78) * mm});
            skLineSegment(sketch, "E19.9.0", {"start": v(-63.28, -64.7) * mm, "end": v(-64.7, -63.28) * mm});
            skLineSegment(sketch, "E19.9.1", {"start": v(-63.28, -64.7) * mm, "end": v(-63.85, -65.27) * mm});
            skLineSegment(sketch, "E19.9.2", {"start": v(-63.85, -65.27) * mm, "end": v(-65.27, -63.85) * mm});
            skLineSegment(sketch, "E19.9.3", {"start": v(-64.7, -63.28) * mm, "end": v(-65.27, -63.85) * mm});
            skLineSegment(sketch, "E19.10.0", {"start": v(-44.38, -78.87) * mm, "end": v(-46.11, -77.87) * mm});
            skLineSegment(sketch, "E19.10.1", {"start": v(-44.38, -78.87) * mm, "end": v(-44.78, -79.57) * mm});
            skLineSegment(sketch, "E19.10.2", {"start": v(-44.78, -79.57) * mm, "end": v(-46.52, -78.57) * mm});
            skLineSegment(sketch, "E19.10.3", {"start": v(-46.11, -77.87) * mm, "end": v(-46.52, -78.57) * mm});
            skLineSegment(sketch, "E19.11.0", {"start": v(-22.46, -87.67) * mm, "end": v(-24.39, -87.15) * mm});
            skLineSegment(sketch, "E19.11.1", {"start": v(-22.46, -87.67) * mm, "end": v(-22.66, -88.45) * mm});
            skLineSegment(sketch, "E19.11.2", {"start": v(-22.66, -88.45) * mm, "end": v(-24.6, -87.93) * mm});
            skLineSegment(sketch, "E19.11.3", {"start": v(-24.39, -87.15) * mm, "end": v(-24.6, -87.93) * mm});
            skLineSegment(sketch, "E19.12.0", {"start": v(1, -90.5) * mm, "end": v(-1, -90.5) * mm});
            skLineSegment(sketch, "E19.12.1", {"start": v(1, -90.5) * mm, "end": v(1, -91.3) * mm});
            skLineSegment(sketch, "E19.12.2", {"start": v(1, -91.3) * mm, "end": v(-1, -91.3) * mm});
            skLineSegment(sketch, "E19.12.3", {"start": v(-1, -90.5) * mm, "end": v(-1, -91.3) * mm});
            skLineSegment(sketch, "E19.13.0", {"start": v(24.39, -87.15) * mm, "end": v(22.46, -87.67) * mm});
            skLineSegment(sketch, "E19.13.1", {"start": v(24.39, -87.15) * mm, "end": v(24.6, -87.93) * mm});
            skLineSegment(sketch, "E19.13.2", {"start": v(24.6, -87.93) * mm, "end": v(22.66, -88.45) * mm});
            skLineSegment(sketch, "E19.13.3", {"start": v(22.46, -87.67) * mm, "end": v(22.66, -88.45) * mm});
            skLineSegment(sketch, "E19.14.0", {"start": v(46.11, -77.87) * mm, "end": v(44.38, -78.87) * mm});
            skLineSegment(sketch, "E19.14.1", {"start": v(46.11, -77.87) * mm, "end": v(46.52, -78.57) * mm});
            skLineSegment(sketch, "E19.14.2", {"start": v(46.52, -78.57) * mm, "end": v(44.78, -79.57) * mm});
            skLineSegment(sketch, "E19.14.3", {"start": v(44.38, -78.87) * mm, "end": v(44.78, -79.57) * mm});
            skLineSegment(sketch, "E19.15.0", {"start": v(64.7, -63.28) * mm, "end": v(63.28, -64.7) * mm});
            skLineSegment(sketch, "E19.15.1", {"start": v(64.7, -63.28) * mm, "end": v(65.27, -63.85) * mm});
            skLineSegment(sketch, "E19.15.2", {"start": v(65.27, -63.85) * mm, "end": v(63.85, -65.27) * mm});
            skLineSegment(sketch, "E19.15.3", {"start": v(63.28, -64.7) * mm, "end": v(63.85, -65.27) * mm});
            skLineSegment(sketch, "E19.16.0", {"start": v(78.87, -44.38) * mm, "end": v(77.87, -46.11) * mm});
            skLineSegment(sketch, "E19.16.1", {"start": v(78.87, -44.38) * mm, "end": v(79.57, -44.78) * mm});
            skLineSegment(sketch, "E19.16.2", {"start": v(79.57, -44.78) * mm, "end": v(78.57, -46.52) * mm});
            skLineSegment(sketch, "E19.16.3", {"start": v(77.87, -46.11) * mm, "end": v(78.57, -46.52) * mm});
            skLineSegment(sketch, "E19.17.0", {"start": v(87.67, -22.46) * mm, "end": v(87.15, -24.39) * mm});
            skLineSegment(sketch, "E19.17.1", {"start": v(87.67, -22.46) * mm, "end": v(88.45, -22.66) * mm});
            skLineSegment(sketch, "E19.17.2", {"start": v(88.45, -22.66) * mm, "end": v(87.93, -24.6) * mm});
            skLineSegment(sketch, "E19.17.3", {"start": v(87.15, -24.39) * mm, "end": v(87.93, -24.6) * mm});
            skLineSegment(sketch, "E19.18.0", {"start": v(90.5, 1) * mm, "end": v(90.5, -1) * mm});
            skLineSegment(sketch, "E19.18.1", {"start": v(90.5, 1) * mm, "end": v(91.3, 1) * mm});
            skLineSegment(sketch, "E19.18.2", {"start": v(91.3, 1) * mm, "end": v(91.3, -1) * mm});
            skLineSegment(sketch, "E19.18.3", {"start": v(90.5, -1) * mm, "end": v(91.3, -1) * mm});
            skLineSegment(sketch, "E19.19.0", {"start": v(87.15, 24.39) * mm, "end": v(87.67, 22.46) * mm});
            skLineSegment(sketch, "E19.19.1", {"start": v(87.15, 24.39) * mm, "end": v(87.93, 24.6) * mm});
            skLineSegment(sketch, "E19.19.2", {"start": v(87.93, 24.6) * mm, "end": v(88.45, 22.66) * mm});
            skLineSegment(sketch, "E19.19.3", {"start": v(87.67, 22.46) * mm, "end": v(88.45, 22.66) * mm});
            skLineSegment(sketch, "E19.20.0", {"start": v(77.87, 46.11) * mm, "end": v(78.87, 44.38) * mm});
            skLineSegment(sketch, "E19.20.1", {"start": v(77.87, 46.11) * mm, "end": v(78.57, 46.52) * mm});
            skLineSegment(sketch, "E19.20.2", {"start": v(78.57, 46.52) * mm, "end": v(79.57, 44.78) * mm});
            skLineSegment(sketch, "E19.20.3", {"start": v(78.87, 44.38) * mm, "end": v(79.57, 44.78) * mm});
            skLineSegment(sketch, "E19.21.0", {"start": v(63.28, 64.7) * mm, "end": v(64.7, 63.28) * mm});
            skLineSegment(sketch, "E19.21.1", {"start": v(63.28, 64.7) * mm, "end": v(63.85, 65.27) * mm});
            skLineSegment(sketch, "E19.21.2", {"start": v(63.85, 65.27) * mm, "end": v(65.27, 63.85) * mm});
            skLineSegment(sketch, "E19.21.3", {"start": v(64.7, 63.28) * mm, "end": v(65.27, 63.85) * mm});
            skLineSegment(sketch, "E19.22.0", {"start": v(44.38, 78.87) * mm, "end": v(46.11, 77.87) * mm});
            skLineSegment(sketch, "E19.22.1", {"start": v(44.38, 78.87) * mm, "end": v(44.78, 79.57) * mm});
            skLineSegment(sketch, "E19.22.2", {"start": v(44.78, 79.57) * mm, "end": v(46.52, 78.57) * mm});
            skLineSegment(sketch, "E19.22.3", {"start": v(46.11, 77.87) * mm, "end": v(46.52, 78.57) * mm});
            skLineSegment(sketch, "E19.23.0", {"start": v(22.46, 87.67) * mm, "end": v(24.39, 87.15) * mm});
            skLineSegment(sketch, "E19.23.1", {"start": v(22.46, 87.67) * mm, "end": v(22.66, 88.45) * mm});
            skLineSegment(sketch, "E19.23.2", {"start": v(22.66, 88.45) * mm, "end": v(24.6, 87.93) * mm});
            skLineSegment(sketch, "E19.23.3", {"start": v(24.39, 87.15) * mm, "end": v(24.6, 87.93) * mm});
            skPoint(sketch, "E19.center", {"position": v(0, 0) * mm});
            skSolve(sketch);
        }
        {
            var Q0;
            {var subQ0=sQuery(id+"F4.wireOp",EDGE,"E15");Q0=makeQuery(id+"F4.imprint","IMPRINT",FACE,{"disambiguationData":[TD([[makeQuery(id+"F4.imprint","IMPRINT",EDGE,{"derivedFrom":subQ0}),1.0]])]});}
            extrude(context, id + "F5", {"entities" : qUnion([Q0]), "operationType" : NewBodyOperationType.REMOVE, "endBound" : BoundingType.THROUGH_ALL, "oppositeDirection" : true, "depth" : 25 * mm});
        }
    });
